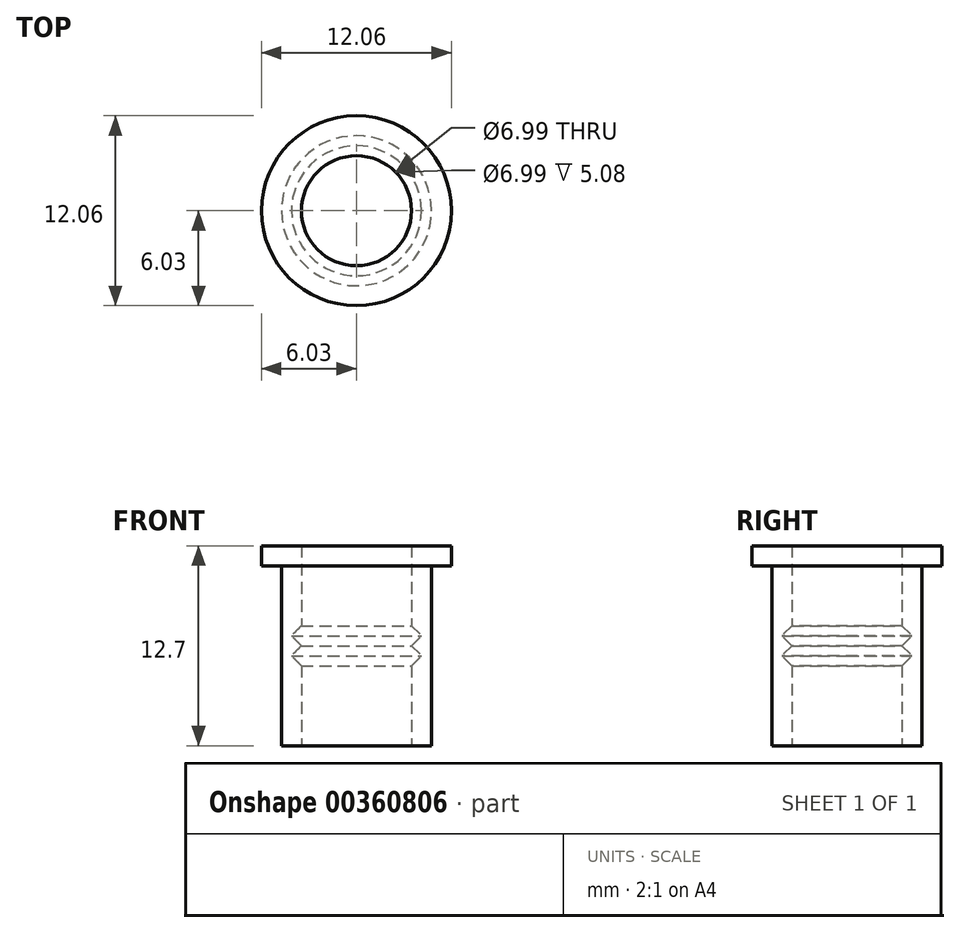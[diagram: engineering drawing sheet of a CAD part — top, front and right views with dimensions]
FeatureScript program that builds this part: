
annotation { "Feature Type Name" : "Feature", "Feature Type Description" : "" }
export const myFeature = defineFeature(function(context is Context, id is Id, definition is map)
    precondition{}
    {
        {
            var Q0;
            Q0=qCreatedBy(makeId("Front.planeOp"),FACE);
            var sketch = newSketch(context, id + "F0", { "sketchPlane" : qUnion([Q0])});
            skLineSegment(sketch, "E0.top", {"start": v(3.5, 12.7) * mm, "end": v(4.76, 12.7) * mm});
            skLineSegment(sketch, "E0.left", {"start": v(0, 0) * mm, "end": v(0, 12.7) * mm});
            skLineSegment(sketch, "E0.right", {"start": v(4.76, 0) * mm, "end": v(4.76, 11.43) * mm});
            skLineSegment(sketch, "E1", {"start": v(3.5, 12.7) * mm, "end": v(3.5, 7.62) * mm});
            skLineSegment(sketch, "E2", {"start": v(3.5, 7.62) * mm, "end": v(4.13, 6.99) * mm});
            skLineSegment(sketch, "E3", {"start": v(4.13, 6.99) * mm, "end": v(3.5, 6.35) * mm});
            skLineSegment(sketch, "E4", {"start": v(3.5, 6.35) * mm, "end": v(4.13, 5.72) * mm});
            skLineSegment(sketch, "E5", {"start": v(4.13, 5.72) * mm, "end": v(3.5, 5.08) * mm});
            skLineSegment(sketch, "E6", {"start": v(3.5, 0) * mm, "end": v(4.76, 0) * mm});
            skLineSegment(sketch, "E7.trimOffspring", {"start": v(3.5, 5.08) * mm, "end": v(3.5, 0) * mm});
            skLineSegment(sketch, "E8.bottom", {"start": v(4.76, 12.7) * mm, "end": v(6.03, 12.7) * mm});
            skLineSegment(sketch, "E8.top", {"start": v(4.76, 11.43) * mm, "end": v(6.03, 11.43) * mm});
            skLineSegment(sketch, "E8.right", {"start": v(6.03, 12.7) * mm, "end": v(6.03, 11.43) * mm});
            skSolve(sketch);
        }
        {
            var Q0;
            Q0=makeQuery(id+"F0.imprint","IMPRINT",FACE,{"disambiguationData":[TD([[makeQuery(id+"F0.imprint","IMPRINT",EDGE,{"derivedFrom":sQuery(id+"F0.wireOp",EDGE,"E0.top")}),-1.0]])]});
            var Q1;
            Q1=sQuery(id+"F0.wireOp",EDGE,"E0.left");
            revolve(context, id + "F1", {"entities" : qUnion([Q0]), "axis" : qUnion([Q1]), "revolveType" : RevolveType.FULL});
        }
    });
